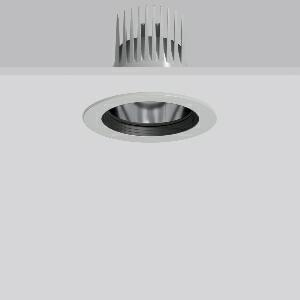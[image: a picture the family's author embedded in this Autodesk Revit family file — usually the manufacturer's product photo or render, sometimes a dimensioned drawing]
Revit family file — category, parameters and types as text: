
# Revit family: heledon_maxi_e_901764_004_76_10cc
name_source: partatom
category: Lighting Fixtures
units: mm (PartAtom-declared; Revit-internal decimal feet)

## family parameters
Cut with Voids When Loaded = No
Host = Face
Light Source = No
Part Type = Normal
Room Calculation Point = No
Round Connector Dimension = Use Diameter
Shared = No

## types (1)
- HELEDON maxi E (1 x LED Modul 930, 4300 lm, 3000)
    Apparent Load = 35 VA
    Approval mark = CE
    CIE Flux Codes = 100 100 100 100 100
    Color Rendering = 90
    Color Temperature = 3000
    Default Elevation = 1800 mm
    Description = Series: HELEDON maxi
Round recessed downlight. Housing: die-cast aluminium, powder-coated. Black plastic ring and recessed LED to prevent glare from the side. Optical assembly with reflector made of MIRO-Silver with 98% total light reflection for outstanding efficiency - can be changed without tools. Best colour rendering index Ra>90. Suitable for Recessed ceiling mounting. Installation without tools thanks to spring fastening system. Including separate LED converter with connecting cable 600 mm.High quality converter without flickering and stroboscopic effect. Through-wiring box (5 pole) available as accessory. The following accessories can be mounted without use of tools: interchangeable lenses, decorative glasses, honeycomb louvre, clear and frosted diffusers, white interchangeable plastic ring. 
Colour: silver
Diameter: 162 mm
Height: 3 mm
Cut-out diameter: 152 mm
Recess height: 200 mm
Luminaire: recess height: 135 mm
Lamp: LED
Socket: without socket
Colour temperature: 3000K
Colour rendering index (CRI): 92
System power: 35 W
Rated luminous flux: 4300 lm
Luminous efficiency: 123 lm/W
Control gear: Converter, dimmable, DALI
Protection class: II
Type of protection: IP 20
    Height = 0 mm  [stored 0 ft]
    Lamp = 1 x LED Modul 930
    Lamp Light Flux = 4300 lm
    Lamp count = 1
    Length = 162 mm
    Lifetime = 50000 h
    Luminous efficacy = 123 lm/W
    Manufacturer = RZB
    ModVariant = No
    Model = 901764.004.76
    Mounting Place = Ceiling
    Mounting Type = Recessed
    Number of Poles = 1
    OnlyDefault = Yes
    Power Factor = 1
    Product Name = HELEDON maxi E
    Product group = Recessed downlights
    ProductGroupID = 402
    Protection Class = Protection class II
    Protection Degree = IP 20
    RLX_Detail_Level = 1
    RLX_Emergency_Light_Flux = 0 lm
    RLX_Emergency_Type = 0
    RLX_Emergency_Type_DB = No
    RlxData = <blob elided: 119465 chars, md5=9e2021c4>
    Socket = socket
    Standby Power = 0 W
    System Light Flux = 4300 lm
    System Power = 35 W
    Type Comments = Product without accessories
    Type Image = 901662.004.jpg
    URL = http://relux.com
    VarID = ---
    Voltage = 230 V
    Voltage Range = 220-240 V
    Weight = 0.00 kg
    Width = 0 mm  [stored 0 ft]

note: [stored X ft] marks values corroborated as IEEE doubles in the binary element streams (Revit-internal decimal feet)

## geometry (parser evidence)
native form markers: Blend x4, Sweep x10
no freeform markers — native parametric forms only
